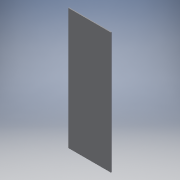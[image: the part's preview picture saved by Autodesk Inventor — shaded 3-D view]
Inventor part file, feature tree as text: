
AUTODESK INVENTOR PART (.ipt)
format: ipt  version: 2019 (Build 230136000, 136)  size: 251,392 bytes
history: native  units: in
note: dims shown in document units (in); Inventor stores cm internally (conversion verified against a paired STEP export)
features: sketch x5, reference x5, extrude x4, projected_geometry x4, other x4, plane x1, mirror x1, helix x1
ambient origin geometry x8: Origin, YZ Plane, XZ Plane, XY Plane, X Axis, Y Axis, Z Axis, Center Point
bodies: Solid1 (feature_tree)
feature tree (25):
  extrude  "Extrusion1"  Depth=0.1575in TaperAngle=0.0deg
  extrude  "Extrusion2"  Depth=0.1575in TaperAngle=0.0deg
  extrude  "Extrusion4"  [1 undecoded]
  extrude  "Extrusion5"  [1 undecoded]
  plane  "Work Plane1"
  mirror  "Mirror1"
  sketch  "Sketch7"
  sketch  "Sketch2"  dims[d0=7.874in d1=0.1575in d2=0.0in]
  sketch  "Sketch3"  dims[d3=0.1575in d4=0.0in d7=0.1575in d8=0.0in]
  reference  "Reference3"
  reference  "Reference4"
  sketch  "Sketch5"  dims[d9=0.1575in d10=0.0in]
  projected_geometry  "Projected Loop1"
  projected_geometry  "Projected Loop2"
  projected_geometry  "Projected Loop3"
  projected_geometry  "Projected Loop4"
  sketch  "Sketch6"
  reference  "Reference7"
  reference  "Reference8"
  reference  "Reference9"
  other  "<userpath>\Documents\CAD Files\Helix DLP\Helix DLP.iam"
  helix  "Helix DLP.iam"  [1 undecoded]
  other  "Maker_jigsaw_template:1"
  other  "Maker_jigsaw_template:2"
  other  "Projector:1"
note: 3 required parameter values undecoded (feature->parameter linkage not recoverable at this tier; creation-order binding heuristic only, values carry confidence <= 0.55)
